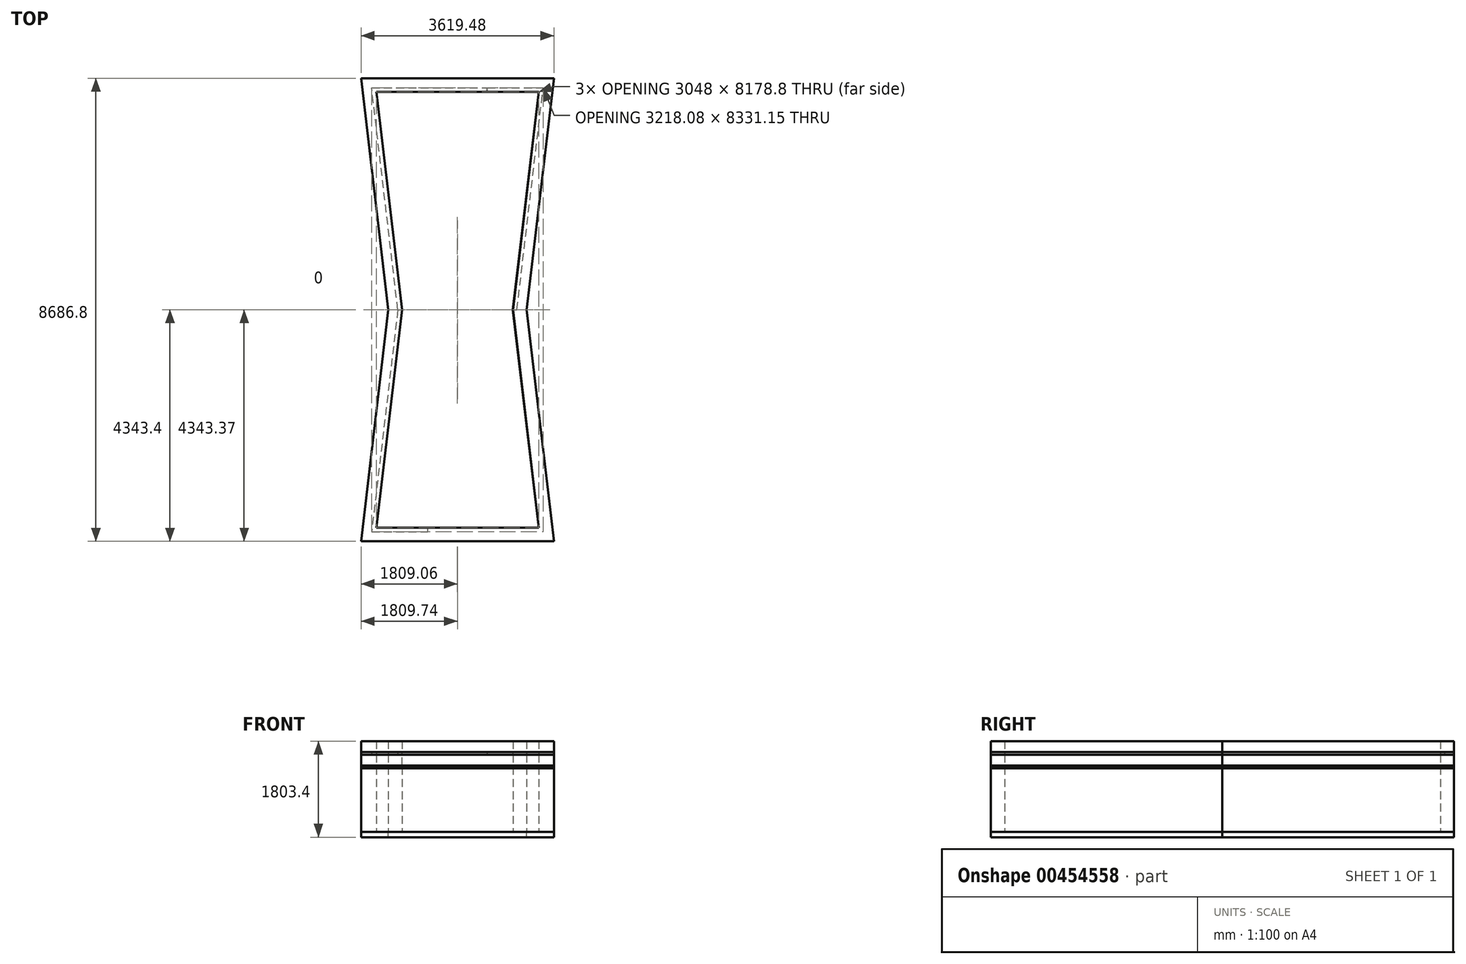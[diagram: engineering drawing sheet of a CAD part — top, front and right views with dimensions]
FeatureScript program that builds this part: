
annotation { "Feature Type Name" : "Feature", "Feature Type Description" : "" }
export const myFeature = defineFeature(function(context is Context, id is Id, definition is map)
    precondition{}
    {
        {
            var Q0;
            Q0=qCreatedBy(makeId("Top.planeOp"),FACE);
            var sketch = newSketch(context, id + "F0", { "sketchPlane" : qUnion([Q0])});
            skLineSegment(sketch, "E0", {"start": v(-1809.74, -4343.4) * mm, "end": v(-1297.16, 0) * mm});
            skLineSegment(sketch, "E1", {"start": v(-1297.16, 0) * mm, "end": v(-1809.74, 4343.4) * mm});
            skLineSegment(sketch, "E2", {"start": v(-1809.74, 4343.4) * mm, "end": v(1809.74, 4343.4) * mm});
            skLineSegment(sketch, "E3", {"start": v(1809.74, 4343.4) * mm, "end": v(1297.16, 0) * mm});
            skLineSegment(sketch, "E4", {"start": v(1297.16, 0) * mm, "end": v(1809.74, -4343.4) * mm});
            skLineSegment(sketch, "E5", {"start": v(1809.74, -4343.4) * mm, "end": v(-1809.74, -4343.4) * mm});
            skLineSegment(sketch, "E6", {"start": v(-1524, 4089.4) * mm, "end": v(1524, 4089.4) * mm});
            skLineSegment(sketch, "E7", {"start": v(1524, 4089.4) * mm, "end": v(1041.4, 0) * mm});
            skLineSegment(sketch, "E8", {"start": v(1041.4, 0) * mm, "end": v(1524, -4089.4) * mm});
            skLineSegment(sketch, "E9", {"start": v(1524, -4089.4) * mm, "end": v(-1524, -4089.4) * mm});
            skLineSegment(sketch, "E10", {"start": v(-1524, -4089.4) * mm, "end": v(-1041.4, 0) * mm});
            skLineSegment(sketch, "E11", {"start": v(-1041.4, 0) * mm, "end": v(-1524, 4089.4) * mm});
            skSolve(sketch);
        }
        {
            var Q0;
            Q0=makeQuery(id+"F0.imprint","IMPRINT",FACE,{"disambiguationData":[TD([[makeQuery(id+"F0.imprint","IMPRINT",EDGE,{"derivedFrom":sQuery(id+"F0.wireOp",EDGE,"E6")}),-1.0]])]});
            var Q1;
            Q1=makeQuery(id+"F0.imprint","IMPRINT",FACE,{"disambiguationData":[TD([[makeQuery(id+"F0.imprint","IMPRINT",EDGE,{"derivedFrom":sQuery(id+"F0.wireOp",EDGE,"E0")}),-1.0]])]});
            extrude(context, id + "F1", {"entities" : qUnion([Q0, Q1]), "oppositeDirection" : true, "depth" : 101.6 * mm});
        }
        {
            var Q0;
            Q0 = qSketchRegion(id + "F0", true);
            extrude(context, id + "F2", {"entities" : qUnion([Q0]), "depth" : 1219.2 * mm});
        }
        {
            var Q0;
            Q0=makeQuery(id+"F2.opExtrude","CAP_FACE",FACE,{"disambiguationData":[OSD([sQuery(id+"F0.wireOp",EDGE,"E0"),sQuery(id+"F0.wireOp",EDGE,"E1"),sQuery(id+"F0.wireOp",EDGE,"E2"),sQuery(id+"F0.wireOp",EDGE,"E3"),sQuery(id+"F0.wireOp",EDGE,"E4"),sQuery(id+"F0.wireOp",EDGE,"E5"),sQuery(id+"F0.wireOp",EDGE,"E6"),sQuery(id+"F0.wireOp",EDGE,"E7"),sQuery(id+"F0.wireOp",EDGE,"E8"),sQuery(id+"F0.wireOp",EDGE,"E9"),sQuery(id+"F0.wireOp",EDGE,"E10"),sQuery(id+"F0.wireOp",EDGE,"E11")])],"isStart":false});
            cPlane(context, id + "F3", {"entities" : qUnion([Q0]), "cplaneType" : CPlaneType.OFFSET, "offset" : 0 * mm, "width" : 152.4 * mm, "height" : 152.4 * mm});
        }
        {
            var Q0;
            Q0=qCreatedBy(id+"F3.planeOp",FACE);
            var sketch = newSketch(context, id + "F4", { "sketchPlane" : qUnion([Q0])});
            skLineSegment(sketch, "E12", {"start": v(-1809.74, -4343.4) * mm, "end": v(-1297.16, 0) * mm});
            skLineSegment(sketch, "E13", {"start": v(-1297.16, 0) * mm, "end": v(-1809.74, 4343.4) * mm});
            skLineSegment(sketch, "E14", {"start": v(-1809.74, 4343.4) * mm, "end": v(1809.74, 4343.4) * mm});
            skLineSegment(sketch, "E15", {"start": v(1809.74, 4343.4) * mm, "end": v(1297.16, 0) * mm});
            skLineSegment(sketch, "E16", {"start": v(1297.16, 0) * mm, "end": v(1809.74, -4343.4) * mm});
            skLineSegment(sketch, "E17", {"start": v(1809.74, -4343.4) * mm, "end": v(-1809.74, -4343.4) * mm});
            skLineSegment(sketch, "E18", {"start": v(-1118.13, 0) * mm, "end": v(-1609.72, -4165.6) * mm});
            skLineSegment(sketch, "E19", {"start": v(-1609.72, -4165.6) * mm, "end": v(-558.8, -4165.6) * mm});
            skLineSegment(sketch, "E20", {"start": v(-558.8, -4165.6) * mm, "end": v(-558.8, -4089.4) * mm});
            skLineSegment(sketch, "E21", {"start": v(-558.8, -4089.4) * mm, "end": v(-1524, -4089.4) * mm});
            skLineSegment(sketch, "E22", {"start": v(-1524, -4089.4) * mm, "end": v(-1041.4, 0) * mm});
            skLineSegment(sketch, "E23", {"start": v(558.8, 4089.4) * mm, "end": v(-1524, 4089.4) * mm});
            skLineSegment(sketch, "E24", {"start": v(-1524, 4089.4) * mm, "end": v(-1041.4, 0) * mm});
            skLineSegment(sketch, "E25", {"start": v(1040, 0) * mm, "end": v(1524, 4089.4) * mm});
            skLineSegment(sketch, "E26", {"start": v(1524, 4089.4) * mm, "end": v(558.8, 4089.4) * mm});
            skLineSegment(sketch, "E27", {"start": v(558.8, 4089.4) * mm, "end": v(557.83, 4165.55) * mm});
            skLineSegment(sketch, "E28", {"start": v(-1118.13, 0) * mm, "end": v(-1041.4, 0) * mm});
            skLineSegment(sketch, "E29", {"start": v(-558.8, -4089.4) * mm, "end": v(1524, -4089.4) * mm});
            skLineSegment(sketch, "E30", {"start": v(1524, -4089.4) * mm, "end": v(1040, 0) * mm});
            skLineSegment(sketch, "E31", {"start": v(1040, 0) * mm, "end": v(1116.25, 0) * mm});
            skLineSegment(sketch, "E32", {"start": v(1116.25, 0) * mm, "end": v(1608.36, 4165.55) * mm});
            skLineSegment(sketch, "E33", {"start": v(557.83, 4165.55) * mm, "end": v(1608.36, 4165.55) * mm});
            skSolve(sketch);
        }
        {
            var Q0;
            Q0=makeQuery(id+"F4.imprint","IMPRINT",FACE,{"disambiguationData":[TD([[makeQuery(id+"F4.imprint","IMPRINT",EDGE,{"derivedFrom":sQuery(id+"F4.wireOp",EDGE,"E12")}),-1.0]])]});
            extrude(context, id + "F5", {"entities" : qUnion([Q0]), "endBound" : BoundingType.SYMMETRIC, "depth" : 50.8 * mm});
        }
        {
            var Q0;
            Q0=makeQuery(id+"F5.opExtrude","CAP_FACE",FACE,{"disambiguationData":[OSD([sQuery(id+"F4.wireOp",EDGE,"E12"),sQuery(id+"F4.wireOp",EDGE,"E13"),sQuery(id+"F4.wireOp",EDGE,"E14"),sQuery(id+"F4.wireOp",EDGE,"E15"),sQuery(id+"F4.wireOp",EDGE,"E16"),sQuery(id+"F4.wireOp",EDGE,"E17"),sQuery(id+"F4.wireOp",EDGE,"E18"),sQuery(id+"F4.wireOp",EDGE,"E19"),sQuery(id+"F4.wireOp",EDGE,"E20"),sQuery(id+"F4.wireOp",EDGE,"E22"),sQuery(id+"F4.wireOp",EDGE,"E23"),sQuery(id+"F4.wireOp",EDGE,"E24"),sQuery(id+"F4.wireOp",EDGE,"E27"),sQuery(id+"F4.wireOp",EDGE,"E28"),sQuery(id+"F4.wireOp",EDGE,"E29"),sQuery(id+"F4.wireOp",EDGE,"E30"),sQuery(id+"F4.wireOp",EDGE,"E31"),sQuery(id+"F4.wireOp",EDGE,"E32"),sQuery(id+"F4.wireOp",EDGE,"E33")])],"isStart":false});
            var sketch = newSketch(context, id + "F6", { "sketchPlane" : qUnion([Q0])});
            skLineSegment(sketch, "E34", {"start": v(-1809.74, -4343.4) * mm, "end": v(-1297.16, 0) * mm});
            skLineSegment(sketch, "E35", {"start": v(-1297.16, 0) * mm, "end": v(-1809.74, 4343.4) * mm});
            skLineSegment(sketch, "E36", {"start": v(-1809.74, 4343.4) * mm, "end": v(1809.74, 4343.4) * mm});
            skLineSegment(sketch, "E37", {"start": v(1809.74, 4343.4) * mm, "end": v(1297.16, 0) * mm});
            skLineSegment(sketch, "E38", {"start": v(1297.16, 0) * mm, "end": v(1809.74, -4343.4) * mm});
            skLineSegment(sketch, "E39", {"start": v(1809.74, -4343.4) * mm, "end": v(-1809.74, -4343.4) * mm});
            skLineSegment(sketch, "E40", {"start": v(-1524, 4089.4) * mm, "end": v(1524, 4089.4) * mm});
            skLineSegment(sketch, "E41", {"start": v(1524, 4089.4) * mm, "end": v(1041.4, 0) * mm});
            skLineSegment(sketch, "E42", {"start": v(1041.4, 0) * mm, "end": v(1524, -4089.4) * mm});
            skLineSegment(sketch, "E43", {"start": v(1524, -4089.4) * mm, "end": v(-1524, -4089.4) * mm});
            skLineSegment(sketch, "E44", {"start": v(-1524, -4089.4) * mm, "end": v(-1041.4, 0) * mm});
            skLineSegment(sketch, "E45", {"start": v(-1041.4, 0) * mm, "end": v(-1524, 4089.4) * mm});
            skSolve(sketch);
        }
        {
            var Q0;
            Q0 = qSketchRegion(id + "F6", true);
            extrude(context, id + "F7", {"entities" : qUnion([Q0]), "depth" : 203.2 * mm});
        }
        {
            var Q0;
            Q0=makeQuery(id+"F7.opExtrude","CAP_FACE",FACE,{"disambiguationData":[OSD([sQuery(id+"F6.wireOp",EDGE,"E34"),sQuery(id+"F6.wireOp",EDGE,"E35"),sQuery(id+"F6.wireOp",EDGE,"E36"),sQuery(id+"F6.wireOp",EDGE,"E37"),sQuery(id+"F6.wireOp",EDGE,"E38"),sQuery(id+"F6.wireOp",EDGE,"E39"),sQuery(id+"F6.wireOp",EDGE,"E40"),sQuery(id+"F6.wireOp",EDGE,"E41"),sQuery(id+"F6.wireOp",EDGE,"E42"),sQuery(id+"F6.wireOp",EDGE,"E43"),sQuery(id+"F6.wireOp",EDGE,"E44"),sQuery(id+"F6.wireOp",EDGE,"E45")])],"isStart":false});
            cPlane(context, id + "F8", {"entities" : qUnion([Q0]), "cplaneType" : CPlaneType.OFFSET, "offset" : 0 * mm, "width" : 152.4 * mm, "height" : 152.4 * mm});
        }
        {
            var Q0;
            Q0=qCreatedBy(id+"F8.planeOp",FACE);
            var sketch = newSketch(context, id + "F9", { "sketchPlane" : qUnion([Q0])});
            skLineSegment(sketch, "E46", {"start": v(-1809.74, -4343.4) * mm, "end": v(-1297.16, 0) * mm});
            skLineSegment(sketch, "E47", {"start": v(-1297.16, 0) * mm, "end": v(-1809.74, 4343.4) * mm});
            skLineSegment(sketch, "E48", {"start": v(-1809.74, 4343.4) * mm, "end": v(1809.74, 4343.4) * mm});
            skLineSegment(sketch, "E49", {"start": v(1809.74, 4343.4) * mm, "end": v(1297.16, 0) * mm});
            skLineSegment(sketch, "E50", {"start": v(1297.16, 0) * mm, "end": v(1809.74, -4343.4) * mm});
            skLineSegment(sketch, "E51", {"start": v(1809.74, -4343.4) * mm, "end": v(-1809.74, -4343.4) * mm});
            skLineSegment(sketch, "E52", {"start": v(-1118.13, 0) * mm, "end": v(-1609.72, 4165.6) * mm});
            skLineSegment(sketch, "E53", {"start": v(-1609.72, 4165.6) * mm, "end": v(558.8, 4165.6) * mm});
            skLineSegment(sketch, "E54", {"start": v(558.8, 4165.6) * mm, "end": v(558.8, 4089.4) * mm});
            skLineSegment(sketch, "E55", {"start": v(558.8, 4089.4) * mm, "end": v(1524, 4089.4) * mm});
            skLineSegment(sketch, "E56", {"start": v(1524, 4089.4) * mm, "end": v(1040, 0) * mm});
            skLineSegment(sketch, "E57", {"start": v(1118.13, 0) * mm, "end": v(1609.72, -4165.6) * mm});
            skLineSegment(sketch, "E58", {"start": v(1609.72, -4165.6) * mm, "end": v(-558.8, -4165.6) * mm});
            skLineSegment(sketch, "E59", {"start": v(-558.8, -4165.6) * mm, "end": v(-558.8, -4089.4) * mm});
            skLineSegment(sketch, "E60", {"start": v(-558.8, -4089.4) * mm, "end": v(-1524, -4089.4) * mm});
            skLineSegment(sketch, "E61", {"start": v(-1524, -4089.4) * mm, "end": v(-1041.4, 0) * mm});
            skLineSegment(sketch, "E62", {"start": v(558.8, 4089.4) * mm, "end": v(-1524, 4089.4) * mm});
            skLineSegment(sketch, "E63", {"start": v(-1524, 4089.4) * mm, "end": v(-1041.4, 0) * mm});
            skLineSegment(sketch, "E64", {"start": v(-1041.4, 0) * mm, "end": v(-1118.13, 0) * mm});
            skLineSegment(sketch, "E65", {"start": v(1116.72, 0) * mm, "end": v(1040, 0) * mm});
            skLineSegment(sketch, "E66", {"start": v(1040, 0) * mm, "end": v(1524, -4089.4) * mm});
            skLineSegment(sketch, "E67", {"start": v(1524, -4089.4) * mm, "end": v(-558.8, -4089.4) * mm});
            skSolve(sketch);
        }
        {
            var Q0;
            Q0=makeQuery(id+"F9.imprint","IMPRINT",FACE,{"disambiguationData":[TD([[makeQuery(id+"F9.imprint","IMPRINT",EDGE,{"derivedFrom":sQuery(id+"F9.wireOp",EDGE,"E46")}),-1.0]])]});
            extrude(context, id + "F10", {"entities" : qUnion([Q0]), "depth" : 50.8 * mm});
        }
        {
            var Q0;
            Q0=makeQuery(id+"F10.opExtrude","CAP_FACE",FACE,{"disambiguationData":[OSD([sQuery(id+"F9.wireOp",EDGE,"E46"),sQuery(id+"F9.wireOp",EDGE,"E47"),sQuery(id+"F9.wireOp",EDGE,"E48"),sQuery(id+"F9.wireOp",EDGE,"E49"),sQuery(id+"F9.wireOp",EDGE,"E50"),sQuery(id+"F9.wireOp",EDGE,"E51"),sQuery(id+"F9.wireOp",EDGE,"E52"),sQuery(id+"F9.wireOp",EDGE,"E53"),sQuery(id+"F9.wireOp",EDGE,"E54"),sQuery(id+"F9.wireOp",EDGE,"E55"),sQuery(id+"F9.wireOp",EDGE,"E56"),sQuery(id+"F9.wireOp",EDGE,"E60"),sQuery(id+"F9.wireOp",EDGE,"E61"),sQuery(id+"F9.wireOp",EDGE,"E64"),sQuery(id+"F9.wireOp",EDGE,"E66"),sQuery(id+"F9.wireOp",EDGE,"E67")])],"isStart":false});
            cPlane(context, id + "F11", {"entities" : qUnion([Q0]), "cplaneType" : CPlaneType.OFFSET, "offset" : 0 * mm, "width" : 152.4 * mm, "height" : 152.4 * mm});
        }
        {
            var Q0;
            Q0=qCreatedBy(id+"F11.planeOp",FACE);
            var sketch = newSketch(context, id + "F12", { "sketchPlane" : qUnion([Q0])});
            skLineSegment(sketch, "E68", {"start": v(-1809.74, -4343.4) * mm, "end": v(-1297.16, 0) * mm});
            skLineSegment(sketch, "E69", {"start": v(-1297.16, 0) * mm, "end": v(-1809.74, 4343.4) * mm});
            skLineSegment(sketch, "E70", {"start": v(-1809.74, 4343.4) * mm, "end": v(1809.74, 4343.4) * mm});
            skLineSegment(sketch, "E71", {"start": v(1809.74, 4343.4) * mm, "end": v(1297.16, 0) * mm});
            skLineSegment(sketch, "E72", {"start": v(1297.16, 0) * mm, "end": v(1809.74, -4343.4) * mm});
            skLineSegment(sketch, "E73", {"start": v(1809.74, -4343.4) * mm, "end": v(-1809.74, -4343.4) * mm});
            skLineSegment(sketch, "E74", {"start": v(-1524, 4089.4) * mm, "end": v(1524, 4089.4) * mm});
            skLineSegment(sketch, "E75", {"start": v(1524, 4089.4) * mm, "end": v(1041.4, 0) * mm});
            skLineSegment(sketch, "E76", {"start": v(1041.4, 0) * mm, "end": v(1524, -4089.4) * mm});
            skLineSegment(sketch, "E77", {"start": v(1524, -4089.4) * mm, "end": v(-1524, -4089.4) * mm});
            skLineSegment(sketch, "E78", {"start": v(-1524, -4089.4) * mm, "end": v(-1041.4, 0) * mm});
            skLineSegment(sketch, "E79", {"start": v(-1041.4, 0) * mm, "end": v(-1524, 4089.4) * mm});
            skSolve(sketch);
        }
        {
            var Q0;
            Q0=makeQuery(id+"F12.imprint","IMPRINT",FACE,{"disambiguationData":[TD([[makeQuery(id+"F12.imprint","IMPRINT",EDGE,{"derivedFrom":sQuery(id+"F12.wireOp",EDGE,"E68")}),-1.0]])]});
            extrude(context, id + "F13", {"entities" : qUnion([Q0]), "depth" : 203.2 * mm});
        }
    });
